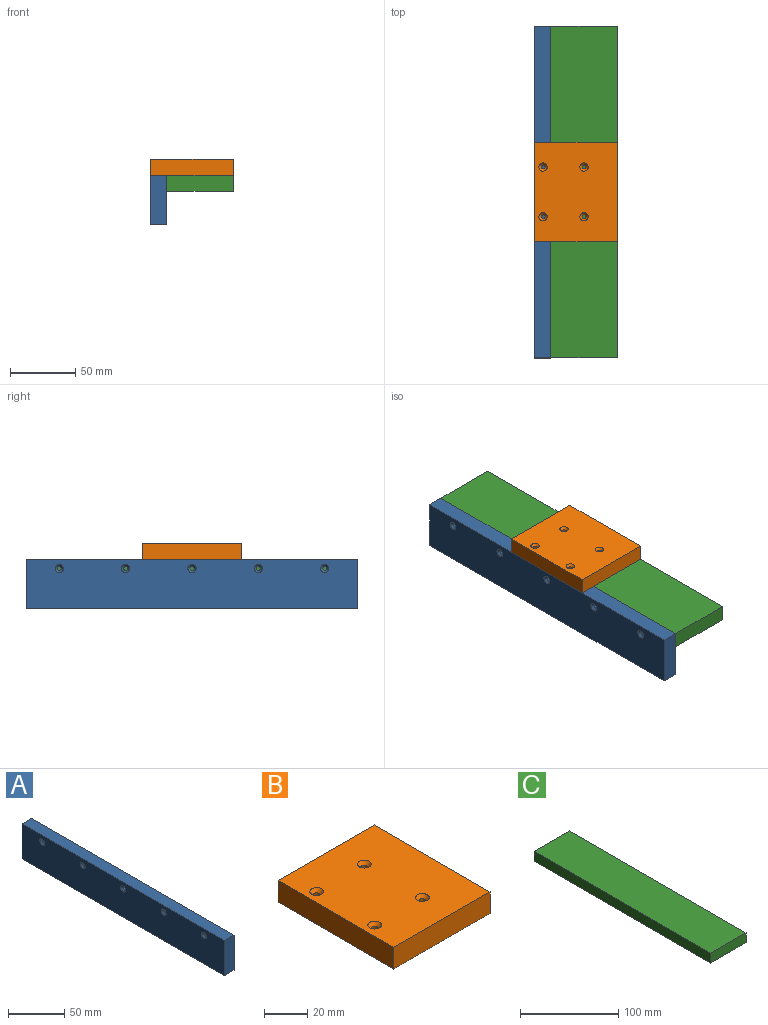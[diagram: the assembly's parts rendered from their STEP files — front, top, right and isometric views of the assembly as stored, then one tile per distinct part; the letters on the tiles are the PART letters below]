
ASSEMBLY  parts=3 mates=2
PART A: 16 faces, bbox 12.3x254x38.1 mm
  f0: plane 254x12.29mm, normal (0,0,1), area 3122.6mm2, adj f1,f3,f4,f5
  f1: plane 254x38.1mm, normal (-1,0,0), area 9519.1mm2, adj f0,f2,f4,f5,f7,f9,f11,f13
  f2: plane 254x12.29mm, normal (0,0,-1), area 3122.6mm2, adj f1,f3,f4,f5
  f3: plane 254x38.1mm, normal (1,0,0), area 9637.8mm2, adj f0,f2,f4,f5,f6,f8,f10,f12
  f4: plane 38.1x12.29mm, normal (0,-1,0), area 468.4mm2, adj f0,f1,f2,f3
  f5: plane 38.1x12.29mm, normal (0,1,0), area 468.4mm2, adj f0,f1,f2,f3
  f6: cylinder r=1.59mm len=10.47mm, axis (-1,0,0), area 104.4mm2, adj f3,f7
  f7: cone r=1.59mm half-angle=41deg, axis (-1,0,0), area 36.2mm2, adj f1,f6
  f8: cylinder r=1.59mm len=10.47mm, axis (-1,0,0), area 104.4mm2, adj f3,f9
  f9: cone r=1.59mm half-angle=41deg, axis (-1,0,0), area 36.2mm2, adj f1,f8
  f10: cylinder r=1.59mm len=10.47mm, axis (-1,0,0), area 104.4mm2, adj f3,f11
  f11: cone r=1.59mm half-angle=41deg, axis (-1,0,0), area 36.2mm2, adj f1,f10
  f12: cylinder r=1.59mm len=10.47mm, axis (-1,0,0), area 104.4mm2, adj f3,f13
  f13: cone r=1.59mm half-angle=41deg, axis (-1,0,0), area 36.2mm2, adj f1,f12
  f14: cylinder r=1.59mm len=10.47mm, axis (-1,0,0), area 104.4mm2, adj f3,f15
  f15: cone r=1.59mm half-angle=41deg, axis (-1,0,0), area 36.2mm2, adj f1,f14
PART B: 14 faces, bbox 63.1x76.2x12.3 mm
  f0: plane 76.2x12.29mm, normal (-1,0,0), area 936.8mm2, adj f1,f3,f4,f5
  f1: plane 76.2x63.09mm, normal (0,0,-1), area 4776.1mm2, adj f0,f2,f4,f5,f6,f8,f10,f12
  f2: plane 76.2x12.29mm, normal (1,0,0), area 936.8mm2, adj f1,f3,f4,f5
  f3: plane 76.2x63.09mm, normal (0,0,1), area 4681.1mm2, adj f0,f2,f4,f5,f7,f9,f11,f13
  f4: plane 63.09x12.29mm, normal (0,-1,0), area 775.6mm2, adj f0,f1,f2,f3
  f5: plane 63.09x12.29mm, normal (0,1,0), area 775.6mm2, adj f0,f1,f2,f3
  f6: cylinder r=1.59mm len=10.47mm, axis (0,0,1), area 104.4mm2, adj f1,f7
  f7: cone r=1.59mm half-angle=41deg, axis (0,0,1), area 36.2mm2, adj f3,f6
  f8: cylinder r=1.59mm len=10.47mm, axis (0,0,1), area 104.4mm2, adj f1,f9
  f9: cone r=1.59mm half-angle=41deg, axis (0,0,1), area 36.2mm2, adj f3,f8
  f10: cylinder r=1.59mm len=10.47mm, axis (0,0,1), area 104.4mm2, adj f1,f11
  f11: cone r=1.59mm half-angle=41deg, axis (0,0,1), area 36.2mm2, adj f3,f10
  f12: cylinder r=1.59mm len=10.47mm, axis (0,0,1), area 104.4mm2, adj f1,f13
  f13: cone r=1.59mm half-angle=41deg, axis (0,0,1), area 36.2mm2, adj f3,f12
PART C: 6 faces, bbox 50.8x254x12.3 mm
  f0: plane 254x50.8mm, normal (0,0,1), area 12903.2mm2, adj f1,f3,f4,f5
  f1: plane 254x12.29mm, normal (-1,0,0), area 3122.6mm2, adj f0,f2,f4,f5
  f2: plane 254x50.8mm, normal (0,0,-1), area 12903.2mm2, adj f1,f3,f4,f5
  f3: plane 254x12.29mm, normal (1,0,0), area 3122.6mm2, adj f0,f2,f4,f5
  f4: plane 50.8x12.29mm, normal (0,-1,0), area 624.5mm2, adj f0,f1,f2,f3
  f5: plane 50.8x12.29mm, normal (0,1,0), area 624.5mm2, adj f0,f1,f2,f3
PLACE A at identity
PLACE B t=(1.53,-88.9,-31.02)mm
PLACE C t=(-5.53,0,-2.68)mm
MATE planar C.f4 <-> A.f4  axis (0,-1,0) through (-28.17,-254,-2.68)mm
MATE planar B.f0 <-> A.f1  axis (-1,0,0) through (-40.46,-127,-2.68)mm
